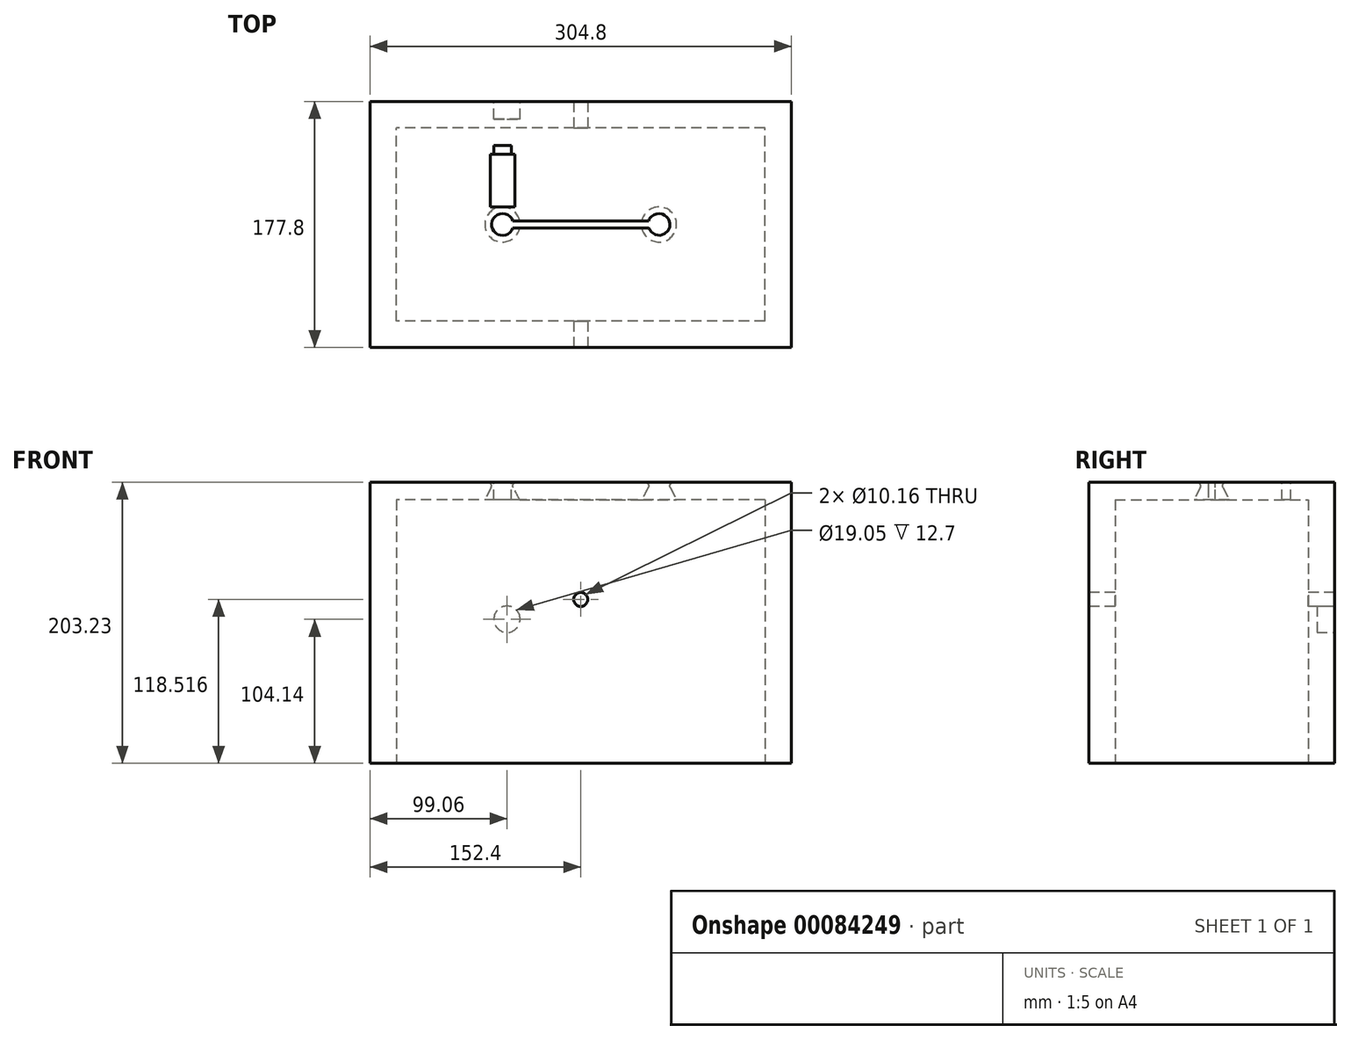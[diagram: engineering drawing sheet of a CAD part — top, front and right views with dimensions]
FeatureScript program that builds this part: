
annotation { "Feature Type Name" : "Feature", "Feature Type Description" : "" }
export const myFeature = defineFeature(function(context is Context, id is Id, definition is map)
    precondition{}
    {
        {
            var Q0;
            Q0=qCreatedBy(makeId("Front.planeOp"),FACE);
            var sketch = newSketch(context, id + "F0", { "sketchPlane" : qUnion([Q0])});
            skLineSegment(sketch, "E0.bottom", {"start": v(152.4, 101.6) * mm, "end": v(-152.4, 101.6) * mm});
            skLineSegment(sketch, "E0.top", {"start": v(152.4, -101.6) * mm, "end": v(-152.4, -101.6) * mm});
            skLineSegment(sketch, "E0.left", {"start": v(152.4, 101.6) * mm, "end": v(152.4, -101.6) * mm});
            skLineSegment(sketch, "E0.right", {"start": v(-152.4, 101.6) * mm, "end": v(-152.4, -101.6) * mm});
            skPoint(sketch, "E0.middle", {"position": v(0, 0) * mm});
            skSolve(sketch);
        }
        {
            var Q0;
            Q0 = qSketchRegion(id + "F0", true);
            extrude(context, id + "F1", {"entities" : qUnion([Q0]), "endBound" : BoundingType.SYMMETRIC, "depth" : 177.8 * mm});
        }
        {
            var Q0;
            Q0=makeQuery(id+"F1.opExtrude","SWEPT_FACE",FACE,{"disambiguationData":[OSD([sQuery(id+"F0.wireOp",EDGE,"E0.top")])]});
            var sketch = newSketch(context, id + "F2", { "sketchPlane" : qUnion([Q0])});
            skLineSegment(sketch, "E1.bottom", {"start": v(133.35, 69.85) * mm, "end": v(-133.35, 69.85) * mm});
            skLineSegment(sketch, "E1.top", {"start": v(133.35, -69.85) * mm, "end": v(-133.35, -69.85) * mm});
            skLineSegment(sketch, "E1.left", {"start": v(133.35, 69.85) * mm, "end": v(133.35, -69.85) * mm});
            skLineSegment(sketch, "E1.right", {"start": v(-133.35, 69.85) * mm, "end": v(-133.35, -69.85) * mm});
            skPoint(sketch, "E1.middle", {"position": v(0, 0) * mm});
            skSolve(sketch);
        }
        {
            var Q0;
            Q0 = qSketchRegion(id + "F2", true);
            extrude(context, id + "F3", {"entities" : qUnion([Q0]), "operationType" : NewBodyOperationType.REMOVE, "oppositeDirection" : true, "depth" : 190.5 * mm});
        }
        {
            var Q0;
            Q0=makeQuery(id+"F1.opExtrude","CAP_FACE",FACE,{"disambiguationData":[OSD([sQuery(id+"F0.wireOp",EDGE,"E0.bottom"),sQuery(id+"F0.wireOp",EDGE,"E0.top"),sQuery(id+"F0.wireOp",EDGE,"E0.left"),sQuery(id+"F0.wireOp",EDGE,"E0.right")])],"isStart":false});
            var sketch = newSketch(context, id + "F4", { "sketchPlane" : qUnion([Q0])});
            skLineSegment(sketch, "E2", {"start": v(-152.4, 101.6) * mm, "end": v(-152.4, 88.9) * mm, "construction": true});
            skLineSegment(sketch, "E3", {"start": v(-152.4, 101.6) * mm, "end": v(-139.7, 101.6) * mm, "construction": true});
            skLineSegment(sketch, "E4", {"start": v(-139.7, 101.6) * mm, "end": v(-139.7, -101.6) * mm, "construction": true});
            skLineSegment(sketch, "E5", {"start": v(-152.4, 88.9) * mm, "end": v(152.4, 88.9) * mm, "construction": true});
            skLineSegment(sketch, "E6", {"start": v(-139.7, 88.9) * mm, "end": v(-53.34, 88.9) * mm, "construction": true});
            skLineSegment(sketch, "E7", {"start": v(-53.34, 88.9) * mm, "end": v(-53.34, 2.54) * mm, "construction": true});
            skCircle(sketch, "E8", {"center": v(-53.34, 2.54) * mm, "radius": 38.1 * mm});
            skSolve(sketch);
        }
        {
            var Q0;
            Q0=makeQuery(id+"F1.opExtrude","SWEPT_FACE",FACE,{"disambiguationData":[OSD([sQuery(id+"F0.wireOp",EDGE,"E0.bottom")])]});
            var sketch = newSketch(context, id + "F5", { "sketchPlane" : qUnion([Q0])});
            skLineSegment(sketch, "E9", {"start": v(50.8, 0) * mm, "end": v(-50.8, 0) * mm, "construction": true});
            skLineSegment(sketch, "E10.0.left", {"start": v(50.8, -2.54) * mm, "end": v(-50.8, -2.54) * mm});
            skLineSegment(sketch, "E10.0.right", {"start": v(50.8, 2.54) * mm, "end": v(-50.8, 2.54) * mm});
            skPoint(sketch, "E11", {"position": v(0, 0) * mm});
            skLineSegment(sketch, "E12", {"start": v(0, 0) * mm, "end": v(-50.8, 0) * mm});
            skLineSegment(sketch, "E13", {"start": v(-50.8, 0) * mm, "end": v(56.62, 0) * mm, "construction": true});
            skArc(sketch, "E14", {"start": v(50.8, 2.54) * mm, "mid": v(62.97, 0) * mm, "end": v(50.8, -2.54) * mm});
            skLineSegment(sketch, "E15", {"start": v(30.06, 2.54) * mm, "end": v(30.06, 0) * mm, "construction": true});
            skLineSegment(sketch, "E16", {"start": v(24.92, -2.54) * mm, "end": v(24.92, 0) * mm, "construction": true});
            skLineSegment(sketch, "E17", {"start": v(50.8, 2.54) * mm, "end": v(56.62, 0) * mm, "construction": true});
            skLineSegment(sketch, "E18", {"start": v(50.8, 2.54) * mm, "end": v(50.8, -2.54) * mm, "construction": true});
            skPoint(sketch, "E19", {"position": v(50.8, 0) * mm});
            skLineSegment(sketch, "E20", {"start": v(0, 2.54) * mm, "end": v(0, -2.54) * mm, "construction": true});
            skArc(sketch, "E21.MirrorCS", {"start": v(-50.8, 2.54) * mm, "mid": v(-62.97, 0) * mm, "end": v(-50.8, -2.54) * mm});
            skSolve(sketch);
        }
        {
            var Q0;
            Q0 = qSketchRegion(id + "F5", true);
            extrude(context, id + "F6", {"entities" : qUnion([Q0]), "operationType" : NewBodyOperationType.REMOVE, "oppositeDirection" : true, "depth" : 25.4 * mm});
        }
        {
            var Q0;
            {var subQ0=sQuery(id+"F0.wireOp",EDGE,"E0.bottom");Q0=makeQuery(id+"F5.imprint","IMPRINT",FACE,{"disambiguationData":[TD([[makeQuery(id+"F5.imprint","IMPRINT",EDGE,{"derivedFrom":makeQuery(id+"F1.opExtrude","CAP_EDGE",EDGE,{"disambiguationData":[OSD([subQ0])],"isStart":true})}),1.0]])]});}
            var sketch = newSketch(context, id + "F7", { "sketchPlane" : qUnion([Q0])});
            skArc(sketch, "E22.0", {"start": v(-50.8, 2.54) * mm, "mid": v(-62.97, 0) * mm, "end": v(-50.8, -2.54) * mm});
            skLineSegment(sketch, "E23", {"start": v(-56.62, 0) * mm, "end": v(-56.62, 31.75) * mm, "construction": true});
            skLineSegment(sketch, "E24.bottom", {"start": v(-47.73, 12.7) * mm, "end": v(-65.5, 12.7) * mm});
            skLineSegment(sketch, "E24.top", {"start": v(-47.73, 50.8) * mm, "end": v(-65.5, 50.8) * mm});
            skLineSegment(sketch, "E24.left", {"start": v(-47.73, 12.7) * mm, "end": v(-47.73, 50.8) * mm});
            skLineSegment(sketch, "E24.right", {"start": v(-65.5, 12.7) * mm, "end": v(-65.5, 50.8) * mm});
            skPoint(sketch, "E24.middle", {"position": v(-56.62, 31.75) * mm});
            skSolve(sketch);
        }
        {
            var Q0;
            Q0=makeQuery(id+"F7.imprint","IMPRINT",FACE,{"disambiguationData":[TD([[makeQuery(id+"F7.imprint","IMPRINT",EDGE,{"derivedFrom":sQuery(id+"F7.wireOp",EDGE,"E24.bottom")}),-1.0]])]});
            extrude(context, id + "F8", {"entities" : qUnion([Q0]), "operationType" : NewBodyOperationType.ADD, "depth" : 0.03 * mm});
        }
        {
            var Q0;
            Q0=makeQuery(id+"F1.opExtrude","SWEPT_FACE",FACE,{"disambiguationData":[OSD([sQuery(id+"F0.wireOp",EDGE,"E0.bottom")])]});
            var sketch = newSketch(context, id + "F9", { "sketchPlane" : qUnion([Q0])});
            skLineSegment(sketch, "E25", {"start": v(-56.62, 50.8) * mm, "end": v(-56.62, 53.97) * mm, "construction": true});
            skLineSegment(sketch, "E26.bottom", {"start": v(-50.27, 57.15) * mm, "end": v(-62.97, 57.15) * mm});
            skLineSegment(sketch, "E26.top", {"start": v(-50.27, 50.8) * mm, "end": v(-62.97, 50.8) * mm});
            skLineSegment(sketch, "E26.left", {"start": v(-50.27, 57.15) * mm, "end": v(-50.27, 50.8) * mm});
            skLineSegment(sketch, "E26.right", {"start": v(-62.97, 57.15) * mm, "end": v(-62.97, 50.8) * mm});
            skPoint(sketch, "E26.middle", {"position": v(-56.62, 53.97) * mm});
            skSolve(sketch);
        }
        {
            var Q0;
            Q0=makeQuery(id+"F9.imprint","IMPRINT",FACE,{"disambiguationData":[TD([[makeQuery(id+"F9.imprint","IMPRINT",EDGE,{"derivedFrom":sQuery(id+"F9.wireOp",EDGE,"E26.bottom")}),1.0]])]});
            extrude(context, id + "F10", {"entities" : qUnion([Q0]), "operationType" : NewBodyOperationType.REMOVE, "oppositeDirection" : true, "depth" : 12.7 * mm});
        }
        {
            var Q0;
            Q0=makeQuery(id+"F1.opExtrude","CAP_FACE",FACE,{"disambiguationData":[OSD([sQuery(id+"F0.wireOp",EDGE,"E0.bottom"),sQuery(id+"F0.wireOp",EDGE,"E0.top"),sQuery(id+"F0.wireOp",EDGE,"E0.left"),sQuery(id+"F0.wireOp",EDGE,"E0.right")])],"isStart":false});
            var sketch = newSketch(context, id + "F11", { "sketchPlane" : qUnion([Q0])});
            skLineSegment(sketch, "E27", {"start": v(0, 101.6) * mm, "end": v(0, 16.92) * mm});
            skPoint(sketch, "E27.endSnap0", {"position": v(0, 101.6) * mm});
            skCircle(sketch, "E28", {"center": v(0, 16.92) * mm, "radius": 5.08 * mm});
            skSolve(sketch);
        }
        {
            var Q0;
            Q0 = qSketchRegion(id + "F11", true);
            extrude(context, id + "F12", {"entities" : qUnion([Q0]), "operationType" : NewBodyOperationType.REMOVE, "endBound" : BoundingType.THROUGH_ALL, "oppositeDirection" : true, "depth" : 25.4 * mm});
        }
        {
            var Q0;
            Q0=makeQuery(id+"F6.boolean.opBoolean","INTERSECT",EDGE,{"derivedFrom":[makeQuery(id+"F3.boolean.opBoolean","COPY",FACE,{"derivedFrom":makeQuery(id+"F3.opExtrude","CAP_FACE",FACE,{"disambiguationData":[OSD([sQuery(id+"F2.wireOp",EDGE,"E1.bottom"),sQuery(id+"F2.wireOp",EDGE,"E1.top"),sQuery(id+"F2.wireOp",EDGE,"E1.left"),sQuery(id+"F2.wireOp",EDGE,"E1.right")])],"isStart":false})}),makeQuery(id+"F6.opExtrude","SWEPT_FACE",FACE,{"disambiguationData":[OSD([sQuery(id+"F5.wireOp",EDGE,"E21.MirrorCS")])]})]});
            var Q1;
            Q1=makeQuery(id+"F6.boolean.opBoolean","INTERSECT",EDGE,{"derivedFrom":[makeQuery(id+"F3.boolean.opBoolean","COPY",FACE,{"derivedFrom":makeQuery(id+"F3.opExtrude","CAP_FACE",FACE,{"disambiguationData":[OSD([sQuery(id+"F2.wireOp",EDGE,"E1.bottom"),sQuery(id+"F2.wireOp",EDGE,"E1.top"),sQuery(id+"F2.wireOp",EDGE,"E1.left"),sQuery(id+"F2.wireOp",EDGE,"E1.right")])],"isStart":false})}),makeQuery(id+"F6.opExtrude","SWEPT_FACE",FACE,{"disambiguationData":[OSD([sQuery(id+"F5.wireOp",EDGE,"E14")])]})]});
            chamfer(context, id + "F13", {"entities" : qUnion([Q0, Q1]), "chamferType" : ChamferType.TWO_OFFSETS, "width1" : 12.7 * mm, "oppositeDirection" : false, "width2" : 6.35 * mm, "tangentPropagation" : true});
        }
        {
            var Q0;
            Q0=makeQuery(id+"F13.opChamfer","BLEND_EDGE",EDGE,{"blendedFrom":[makeQuery(id+"F6.boolean.opBoolean","INTERSECT",EDGE,{"derivedFrom":[makeQuery(id+"F3.boolean.opBoolean","COPY",FACE,{"derivedFrom":makeQuery(id+"F3.opExtrude","CAP_FACE",FACE,{"disambiguationData":[OSD([sQuery(id+"F2.wireOp",EDGE,"E1.bottom"),sQuery(id+"F2.wireOp",EDGE,"E1.top"),sQuery(id+"F2.wireOp",EDGE,"E1.left"),sQuery(id+"F2.wireOp",EDGE,"E1.right")])],"isStart":false})}),makeQuery(id+"F6.opExtrude","SWEPT_FACE",FACE,{"disambiguationData":[OSD([sQuery(id+"F5.wireOp",EDGE,"E21.MirrorCS")])]})]}),makeQuery(id+"F1.opExtrude","SWEPT_FACE",FACE,{"disambiguationData":[OSD([sQuery(id+"F0.wireOp",EDGE,"E0.bottom")])]})],"blendedInto":[makeQuery(id+"F1.opExtrude","SWEPT_FACE",FACE,{"disambiguationData":[OSD([sQuery(id+"F0.wireOp",EDGE,"E0.bottom")])]})]});
            var Q1;
            Q1=makeQuery(id+"F13.opChamfer","BLEND_EDGE",EDGE,{"blendedFrom":[makeQuery(id+"F6.boolean.opBoolean","INTERSECT",EDGE,{"derivedFrom":[makeQuery(id+"F3.boolean.opBoolean","COPY",FACE,{"derivedFrom":makeQuery(id+"F3.opExtrude","CAP_FACE",FACE,{"disambiguationData":[OSD([sQuery(id+"F2.wireOp",EDGE,"E1.bottom"),sQuery(id+"F2.wireOp",EDGE,"E1.top"),sQuery(id+"F2.wireOp",EDGE,"E1.left"),sQuery(id+"F2.wireOp",EDGE,"E1.right")])],"isStart":false})}),makeQuery(id+"F6.opExtrude","SWEPT_FACE",FACE,{"disambiguationData":[OSD([sQuery(id+"F5.wireOp",EDGE,"E14")])]})]}),makeQuery(id+"F1.opExtrude","SWEPT_FACE",FACE,{"disambiguationData":[OSD([sQuery(id+"F0.wireOp",EDGE,"E0.bottom")])]})],"blendedInto":[makeQuery(id+"F1.opExtrude","SWEPT_FACE",FACE,{"disambiguationData":[OSD([sQuery(id+"F0.wireOp",EDGE,"E0.bottom")])]})]});
            fillet(context, id + "F14", {"entities" : qUnion([Q0, Q1]), "radius" : 2.54 * mm, "tangentPropagation" : true, "allowEdgeOverflow" : false});
        }
        {
            var Q0;
            Q0=makeQuery(id+"F1.opExtrude","CAP_FACE",FACE,{"disambiguationData":[OSD([sQuery(id+"F0.wireOp",EDGE,"E0.bottom"),sQuery(id+"F0.wireOp",EDGE,"E0.top"),sQuery(id+"F0.wireOp",EDGE,"E0.left"),sQuery(id+"F0.wireOp",EDGE,"E0.right")])],"isStart":true});
            var sketch = newSketch(context, id + "F15", { "sketchPlane" : qUnion([Q0])});
            skLineSegment(sketch, "E29.0", {"start": v(53.34, 88.9) * mm, "end": v(53.34, 2.54) * mm, "construction": true});
            skCircle(sketch, "E30", {"center": v(53.34, 2.54) * mm, "radius": 9.53 * mm});
            skSolve(sketch);
        }
        {
            var Q0;
            Q0 = qSketchRegion(id + "F15", true);
            extrude(context, id + "F16", {"entities" : qUnion([Q0]), "operationType" : NewBodyOperationType.REMOVE, "oppositeDirection" : true, "depth" : 12.7 * mm});
        }
    });
